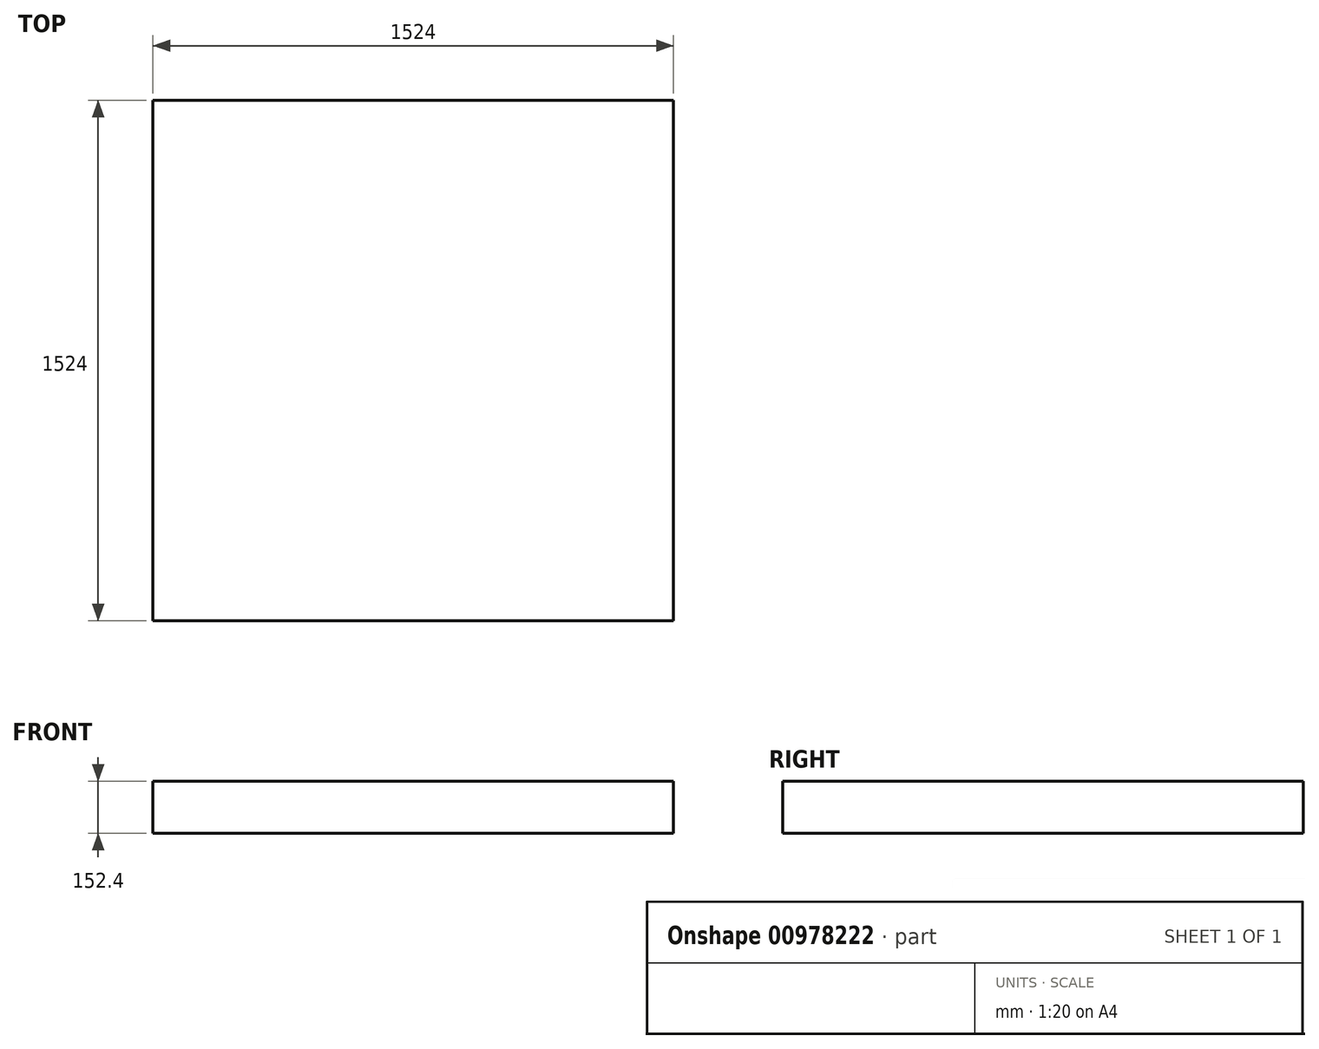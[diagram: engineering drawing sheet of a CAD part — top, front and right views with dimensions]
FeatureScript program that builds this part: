
annotation { "Feature Type Name" : "Feature", "Feature Type Description" : "" }
export const myFeature = defineFeature(function(context is Context, id is Id, definition is map)
    precondition{}
    {
        {
            var Q0;
            Q0=qCreatedBy(makeId("Top.planeOp"),FACE);
            var sketch = newSketch(context, id + "F0", { "sketchPlane" : qUnion([Q0])});
            skLineSegment(sketch, "E0.bottom", {"start": v(762, -762) * mm, "end": v(-762, -762) * mm});
            skLineSegment(sketch, "E0.top", {"start": v(762, 762) * mm, "end": v(-762, 762) * mm});
            skLineSegment(sketch, "E0.left", {"start": v(762, -762) * mm, "end": v(762, 762) * mm});
            skLineSegment(sketch, "E0.right", {"start": v(-762, -762) * mm, "end": v(-762, 762) * mm});
            skPoint(sketch, "E0.middle", {"position": v(0, 0) * mm});
            skSolve(sketch);
        }
        {
            var Q0;
            Q0=makeQuery(id+"F0.imprint","IMPRINT",FACE,{"disambiguationData":[TD([[makeQuery(id+"F0.imprint","IMPRINT",EDGE,{"derivedFrom":sQuery(id+"F0.wireOp",EDGE,"E0.bottom")}),-1.0]])]});
            extrude(context, id + "F1", {"entities" : qUnion([Q0]), "oppositeDirection" : true, "depth" : 152.4 * mm, "offsetDistance" : 25.4 * mm});
        }
        {
            var Q0;
            Q0=makeQuery(id+"F1.opExtrude","CAP_FACE",FACE,{"disambiguationData":[OSD([sQuery(id+"F0.wireOp",EDGE,"E0.bottom"),sQuery(id+"F0.wireOp",EDGE,"E0.top"),sQuery(id+"F0.wireOp",EDGE,"E0.left"),sQuery(id+"F0.wireOp",EDGE,"E0.right")])],"isStart":true});
            var sketch = newSketch(context, id + "F2", { "sketchPlane" : qUnion([Q0])});
            skCircle(sketch, "E1", {"center": v(-1320.8, 0) * mm, "radius": 88.9 * mm});
            skSolve(sketch);
        }
        {
            var Q0;
            Q0=makeQuery(id+"F2.imprint","IMPRINT",FACE,{"disambiguationData":[TD([[makeQuery(id+"F2.imprint","IMPRINT",EDGE,{"derivedFrom":sQuery(id+"F2.wireOp",EDGE,"E1")}),1.0]])]});
            extrude(context, id + "F3", {"entities" : qUnion([Q0]), "operationType" : NewBodyOperationType.REMOVE, "oppositeDirection" : true, "depth" : 2.54 * mm, "offsetDistance" : 25.4 * mm});
        }
    });
